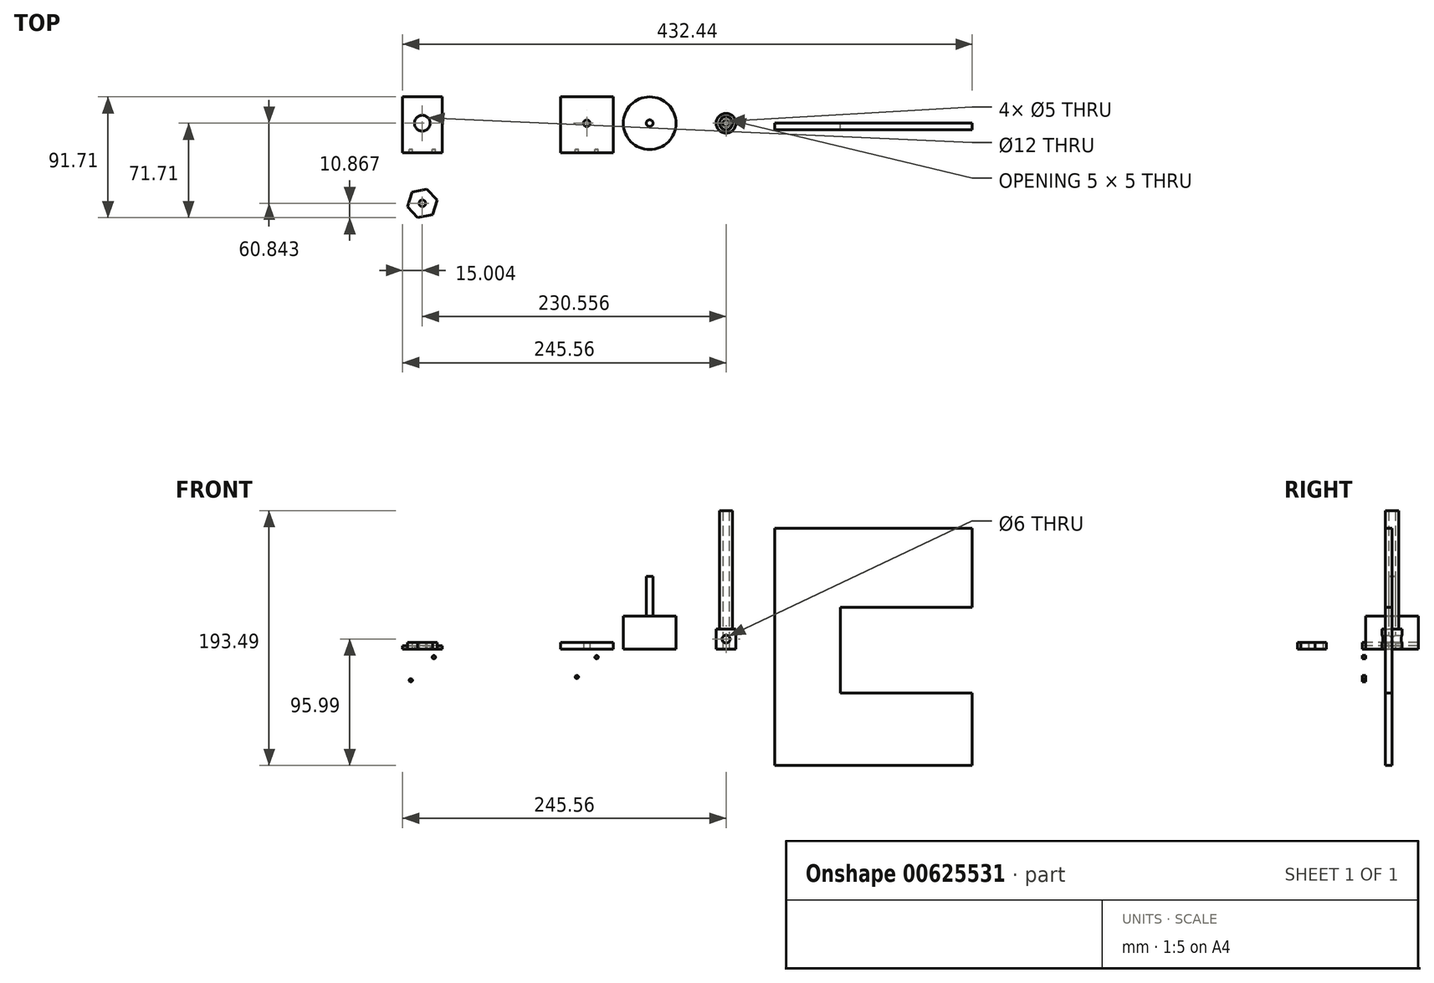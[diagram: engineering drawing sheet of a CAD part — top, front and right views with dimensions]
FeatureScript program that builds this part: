
annotation { "Feature Type Name" : "Feature", "Feature Type Description" : "" }
export const myFeature = defineFeature(function(context is Context, id is Id, definition is map)
    precondition{}
    {
        {
            var Q0;
            Q0=qCreatedBy(makeId("Top.planeOp"),FACE);
            var sketch = newSketch(context, id + "F0", { "sketchPlane" : qUnion([Q0])});
            skCircle(sketch, "E0", {"center": v(0, 0) * mm, "radius": 2.5 * mm});
            skCircle(sketch, "E1", {"center": v(0, 0) * mm, "radius": 7.5 * mm});
            skLineSegment(sketch, "E2", {"start": v(-20, 7.5) * mm, "end": v(20, 7.5) * mm});
            skCircle(sketch, "E3", {"center": v(-57.97, 0) * mm, "radius": 20 * mm});
            skLineSegment(sketch, "E4.bottom", {"start": v(-125.74, 20) * mm, "end": v(-85.74, 20) * mm});
            skLineSegment(sketch, "E4.top", {"start": v(-125.74, -20) * mm, "end": v(-85.74, -20) * mm});
            skLineSegment(sketch, "E4.left", {"start": v(-125.74, 20) * mm, "end": v(-125.74, -20) * mm});
            skLineSegment(sketch, "E4.right", {"start": v(-85.74, 20) * mm, "end": v(-85.74, -20) * mm});
            skPoint(sketch, "E4.middle", {"position": v(-105.74, 0) * mm});
            skCircle(sketch, "E5", {"center": v(-105.74, 0) * mm, "radius": 2.5 * mm});
            skLineSegment(sketch, "E6.bottom", {"start": v(-215.56, 20) * mm, "end": v(-245.56, 20) * mm});
            skLineSegment(sketch, "E6.top", {"start": v(-215.56, -20) * mm, "end": v(-245.56, -20) * mm});
            skLineSegment(sketch, "E6.left", {"start": v(-215.56, 20) * mm, "end": v(-215.56, -20) * mm});
            skLineSegment(sketch, "E6.right", {"start": v(-245.56, 20) * mm, "end": v(-245.56, -20) * mm});
            skCircle(sketch, "E7", {"center": v(-230.56, 0) * mm, "radius": 6 * mm});
            skPoint(sketch, "E7.centerSnap0", {"position": v(-230.56, 20) * mm});
            skCircle(sketch, "E8.cCircle", {"center": v(-230.56, -60.84) * mm, "radius": 9.88 * mm, "construction": true});
            skLineSegment(sketch, "E8.0", {"start": v(-219.4, -58.45) * mm, "end": v(-222.9, -69.3) * mm});
            skLineSegment(sketch, "E8.1", {"start": v(-222.9, -69.3) * mm, "end": v(-234.06, -71.7) * mm});
            skLineSegment(sketch, "E8.2", {"start": v(-234.06, -71.7) * mm, "end": v(-241.71, -63.24) * mm});
            skLineSegment(sketch, "E8.3", {"start": v(-241.71, -63.24) * mm, "end": v(-238.21, -52.38) * mm});
            skLineSegment(sketch, "E8.4", {"start": v(-238.21, -52.38) * mm, "end": v(-227.05, -49.98) * mm});
            skLineSegment(sketch, "E8.5", {"start": v(-227.05, -49.98) * mm, "end": v(-219.4, -58.45) * mm});
            skPoint(sketch, "E8.0.midPoint", {"position": v(-221.15, -63.88) * mm});
            skCircle(sketch, "E9", {"center": v(-230.56, -60.84) * mm, "radius": 2.5 * mm});
            skSolve(sketch);
        }
        {
            var Q0;
            Q0=makeQuery(id+"F0.imprint","IMPRINT",FACE,{"disambiguationData":[TD([[makeQuery(id+"F0.imprint","IMPRINT",EDGE,{"derivedFrom":sQuery(id+"F0.wireOp",EDGE,"E0")}),-1.0]])]});
            extrude(context, id + "F1", {"entities" : qUnion([Q0]), "depth" : 15 * mm, "offsetDistance" : 25 * mm});
        }
        {
            var Q0;
            Q0=makeQuery(id+"F1.opExtrude","CAP_FACE",FACE,{"disambiguationData":[OSD([sQuery(id+"F0.wireOp",EDGE,"E0"),sQuery(id+"F0.wireOp",EDGE,"E1")])],"isStart":false});
            var sketch = newSketch(context, id + "F2", { "sketchPlane" : qUnion([Q0])});
            skCircle(sketch, "E10", {"center": v(0, 0) * mm, "radius": 5 * mm});
            skSolve(sketch);
        }
        {
            var Q0;
            Q0=makeQuery(id+"F2.imprint","IMPRINT",FACE,{"disambiguationData":[TD([[makeQuery(id+"F2.imprint","IMPRINT",EDGE,{"derivedFrom":sQuery(id+"F2.wireOp",EDGE,"E10")}),1.0]])]});
            extrude(context, id + "F3", {"entities" : qUnion([Q0]), "operationType" : NewBodyOperationType.ADD, "depth" : 90 * mm, "offsetDistance" : 25 * mm});
        }
        {
            var Q0;
            Q0=sQuery(id+"F0.wireOp",EDGE,"E2");
            extrude(context, id + "F4", {"bodyType" : ToolBodyType.SURFACE, "surfaceEntities" : qUnion([Q0]), "depth" : 15 * mm, "offsetDistance" : 25 * mm});
        }
        {
            var Q0;
            Q0=makeQuery(id+"F4.opExtrude","SWEPT_FACE",FACE,{"disambiguationData":[OSD([sQuery(id+"F0.wireOp",EDGE,"E2")])]});
            var sketch = newSketch(context, id + "F5", { "sketchPlane" : qUnion([Q0])});
            skCircle(sketch, "E11", {"center": v(0, 7.5) * mm, "radius": 3 * mm});
            skPoint(sketch, "E11.centerSnap0", {"position": v(-20, 7.5) * mm});
            skSolve(sketch);
        }
        {
            var Q0;
            Q0=makeQuery(id+"F5.imprint","IMPRINT",FACE,{"disambiguationData":[TD([[makeQuery(id+"F5.imprint","IMPRINT",EDGE,{"derivedFrom":sQuery(id+"F5.wireOp",EDGE,"E11")}),1.0]])]});
            extrude(context, id + "F6", {"entities" : qUnion([Q0]), "operationType" : NewBodyOperationType.REMOVE, "endBound" : BoundingType.THROUGH_ALL, "depth" : 25 * mm, "offsetDistance" : 25 * mm});
        }
        {
            var Q0;
            Q0=makeQuery(id+"F0.imprint","IMPRINT",FACE,{"disambiguationData":[TD([[makeQuery(id+"F0.imprint","IMPRINT",EDGE,{"derivedFrom":sQuery(id+"F0.wireOp",EDGE,"E3")}),1.0]])]});
            extrude(context, id + "F7", {"entities" : qUnion([Q0]), "depth" : 25 * mm, "offsetDistance" : 25 * mm});
        }
        {
            var Q0;
            Q0=makeQuery(id+"F7.opExtrude","CAP_FACE",FACE,{"disambiguationData":[OSD([sQuery(id+"F0.wireOp",EDGE,"E3")])],"isStart":false});
            var sketch = newSketch(context, id + "F8", { "sketchPlane" : qUnion([Q0])});
            skCircle(sketch, "E12", {"center": v(-57.97, 0) * mm, "radius": 2.5 * mm});
            skSolve(sketch);
        }
        {
            var Q0;
            Q0=makeQuery(id+"F8.imprint","IMPRINT",FACE,{"disambiguationData":[TD([[makeQuery(id+"F8.imprint","IMPRINT",EDGE,{"derivedFrom":sQuery(id+"F8.wireOp",EDGE,"E12")}),1.0]])]});
            extrude(context, id + "F9", {"entities" : qUnion([Q0]), "operationType" : NewBodyOperationType.ADD, "depth" : 30 * mm, "offsetDistance" : 25 * mm});
        }
        {
            var Q0;
            Q0=makeQuery(id+"F0.imprint","IMPRINT",FACE,{"disambiguationData":[TD([[makeQuery(id+"F0.imprint","IMPRINT",EDGE,{"derivedFrom":sQuery(id+"F0.wireOp",EDGE,"E4.bottom")}),-1.0]])]});
            extrude(context, id + "F10", {"entities" : qUnion([Q0]), "depth" : 5 * mm, "offsetDistance" : 25 * mm});
        }
        {
            var Q0;
            Q0=makeQuery(id+"F10.opExtrude","CAP_FACE",FACE,{"disambiguationData":[OSD([sQuery(id+"F0.wireOp",EDGE,"E4.bottom"),sQuery(id+"F0.wireOp",EDGE,"E4.top"),sQuery(id+"F0.wireOp",EDGE,"E4.left"),sQuery(id+"F0.wireOp",EDGE,"E4.right"),sQuery(id+"F0.wireOp",EDGE,"E5")])],"isStart":false});
            var sketch = newSketch(context, id + "F11", { "sketchPlane" : qUnion([Q0])});
            skLineSegment(sketch, "E13.bottom", {"start": v(-125.74, -20) * mm, "end": v(-85.74, -20) * mm});
            skLineSegment(sketch, "E13.top", {"start": v(-125.74, -22.5) * mm, "end": v(-85.74, -22.5) * mm});
            skLineSegment(sketch, "E13.left", {"start": v(-125.74, -20) * mm, "end": v(-125.74, -22.5) * mm});
            skLineSegment(sketch, "E13.right", {"start": v(-85.74, -20) * mm, "end": v(-85.74, -22.5) * mm});
            skSolve(sketch);
        }
        {
            var Q0;
            Q0=makeQuery(id+"F11.imprint","IMPRINT",FACE,{"disambiguationData":[TD([[makeQuery(id+"F11.imprint","IMPRINT",EDGE,{"derivedFrom":sQuery(id+"F11.wireOp",EDGE,"E13.bottom")}),-1.0]])]});
            extrude(context, id + "F12", {"entities" : qUnion([Q0]), "operationType" : NewBodyOperationType.ADD, "oppositeDirection" : true, "depth" : 32.5 * mm, "offsetDistance" : 25 * mm});
        }
        {
            var Q0;
            Q0=qCreatedBy(makeId("Front.planeOp"),FACE);
            var sketch = newSketch(context, id + "F13", { "sketchPlane" : qUnion([Q0])});
            skLineSegment(sketch, "E14.bottom", {"start": v(36.88, 91.5) * mm, "end": v(186.88, 91.5) * mm});
            skLineSegment(sketch, "E14.top", {"start": v(36.88, -88.5) * mm, "end": v(186.88, -88.5) * mm});
            skLineSegment(sketch, "E14.left", {"start": v(36.88, 91.5) * mm, "end": v(36.88, -88.5) * mm});
            skLineSegment(sketch, "E14.right", {"start": v(186.88, 91.5) * mm, "end": v(186.88, -88.5) * mm});
            skLineSegment(sketch, "E15", {"start": v(186.88, 31.5) * mm, "end": v(86.88, 31.5) * mm});
            skLineSegment(sketch, "E16", {"start": v(186.88, -33.5) * mm, "end": v(86.88, -33.5) * mm});
            skLineSegment(sketch, "E17", {"start": v(86.88, 31.5) * mm, "end": v(86.88, -33.5) * mm});
            skLineSegment(sketch, "E18.bottom", {"start": v(272.35, 206.17) * mm, "end": v(332.35, 206.17) * mm});
            skLineSegment(sketch, "E18.top", {"start": v(272.35, 156.17) * mm, "end": v(332.35, 156.17) * mm});
            skLineSegment(sketch, "E18.left", {"start": v(272.35, 206.17) * mm, "end": v(272.35, 156.17) * mm});
            skLineSegment(sketch, "E18.right", {"start": v(332.35, 206.17) * mm, "end": v(332.35, 156.17) * mm});
            skCircle(sketch, "E19", {"center": v(322.35, 196.17) * mm, "radius": 3 * mm});
            skLineSegment(sketch, "E20", {"start": v(272.35, 181.17) * mm, "end": v(332.35, 181.17) * mm, "construction": true});
            skLineSegment(sketch, "E21", {"start": v(302.35, 156.17) * mm, "end": v(302.35, 206.17) * mm, "construction": true});
            skCircle(sketch, "E22.MirrorC", {"center": v(282.35, 196.17) * mm, "radius": 3 * mm});
            skCircle(sketch, "E23.MirrorC", {"center": v(282.35, 166.17) * mm, "radius": 3 * mm});
            skCircle(sketch, "E24.MirrorC", {"center": v(322.35, 166.17) * mm, "radius": 3 * mm});
            skSolve(sketch);
        }
        {
            var Q0;
            {var subQ1=sQuery(id+"F13.wireOp",EDGE,"E14.bottom");Q0=makeQuery(id+"F13.imprint","IMPRINT",FACE,{"disambiguationData":[TD([[makeQuery(id+"F13.imprint","IMPRINT",EDGE,{"derivedFrom":subQ1}),-1.0]])]});}
            extrude(context, id + "F14", {"entities" : qUnion([Q0]), "depth" : 5 * mm, "offsetDistance" : 25 * mm});
        }
        {
            var Q0;
            Q0=makeQuery(id+"F14.opExtrude","CAP_FACE",FACE,{"disambiguationData":[OSD([sQuery(id+"F13.wireOp",EDGE,"E14.bottom"),sQuery(id+"F13.wireOp",EDGE,"E14.top"),sQuery(id+"F13.wireOp",EDGE,"E14.left"),sQuery(id+"F13.wireOp",EDGE,"E14.right"),sQuery(id+"F13.wireOp",EDGE,"E15"),sQuery(id+"F13.wireOp",EDGE,"E16"),sQuery(id+"F13.wireOp",EDGE,"E17")])],"isStart":false});
            var sketch = newSketch(context, id + "F15", { "sketchPlane" : qUnion([Q0])});
            skLineSegment(sketch, "E25", {"start": v(186.88, 59) * mm, "end": v(86.88, 59) * mm});
            skLineSegment(sketch, "E26", {"start": v(86.88, 59) * mm, "end": v(86.88, 31.5) * mm});
            skLineSegment(sketch, "E27", {"start": v(186.88, -33.5) * mm, "end": v(86.88, -33.5) * mm});
            skLineSegment(sketch, "E28", {"start": v(86.88, -33.5) * mm, "end": v(86.88, -33.5) * mm});
            skLineSegment(sketch, "E29", {"start": v(86.88, 59) * mm, "end": v(86.88, 91.5) * mm});
            skLineSegment(sketch, "E30", {"start": v(86.88, 91.5) * mm, "end": v(86.88, -88.5) * mm});
            skSolve(sketch);
        }
        {
            var Q0;
            Q0=makeQuery(id+"F0.imprint","IMPRINT",FACE,{"disambiguationData":[TD([[makeQuery(id+"F0.imprint","IMPRINT",EDGE,{"derivedFrom":sQuery(id+"F0.wireOp",EDGE,"E6.bottom")}),1.0]])]});
            extrude(context, id + "F16", {"entities" : qUnion([Q0]), "depth" : 2.5 * mm, "offsetDistance" : 25 * mm});
        }
        {
            var Q0;
            Q0=makeQuery(id+"F16.opExtrude","CAP_FACE",FACE,{"disambiguationData":[OSD([sQuery(id+"F0.wireOp",EDGE,"E6.bottom"),sQuery(id+"F0.wireOp",EDGE,"E6.top"),sQuery(id+"F0.wireOp",EDGE,"E6.left"),sQuery(id+"F0.wireOp",EDGE,"E6.right"),sQuery(id+"F0.wireOp",EDGE,"E7")])],"isStart":false});
            var sketch = newSketch(context, id + "F17", { "sketchPlane" : qUnion([Q0])});
            skLineSegment(sketch, "E31.bottom", {"start": v(-245.56, -20) * mm, "end": v(-215.56, -20) * mm});
            skLineSegment(sketch, "E31.top", {"start": v(-245.56, -22.5) * mm, "end": v(-215.56, -22.5) * mm});
            skLineSegment(sketch, "E31.left", {"start": v(-245.56, -20) * mm, "end": v(-245.56, -22.5) * mm});
            skLineSegment(sketch, "E31.right", {"start": v(-215.56, -20) * mm, "end": v(-215.56, -22.5) * mm});
            skSolve(sketch);
        }
        {
            var Q0;
            Q0=makeQuery(id+"F17.imprint","IMPRINT",FACE,{"disambiguationData":[TD([[makeQuery(id+"F17.imprint","IMPRINT",EDGE,{"derivedFrom":sQuery(id+"F17.wireOp",EDGE,"E31.bottom")}),1.0]])]});
            extrude(context, id + "F18", {"entities" : qUnion([Q0]), "operationType" : NewBodyOperationType.ADD, "oppositeDirection" : true, "depth" : 32.5 * mm, "offsetDistance" : 25 * mm});
        }
        {
            var Q0;
            Q0=makeQuery(id+"F0.imprint","IMPRINT",FACE,{"disambiguationData":[TD([[makeQuery(id+"F0.imprint","IMPRINT",EDGE,{"derivedFrom":sQuery(id+"F0.wireOp",EDGE,"E8.0")}),-1.0]])]});
            extrude(context, id + "F19", {"entities" : qUnion([Q0]), "depth" : 5 * mm, "offsetDistance" : 25 * mm});
        }
        {
            var Q0;
            Q0=makeQuery(id+"F12.opExtrude","SWEPT_FACE",FACE,{"disambiguationData":[OSD([sQuery(id+"F11.wireOp",EDGE,"E13.bottom")])]});
            var sketch = newSketch(context, id + "F20", { "sketchPlane" : qUnion([Q0])});
            skCircle(sketch, "E32", {"center": v(113.24, -6.25) * mm, "radius": 1.25 * mm});
            skLineSegment(sketch, "E33", {"start": v(105.74, 0) * mm, "end": v(105.74, -27.5) * mm, "construction": true});
            skLineSegment(sketch, "E34", {"start": v(125.74, -13.75) * mm, "end": v(85.74, -13.75) * mm, "construction": true});
            skCircle(sketch, "E35.MirrorC", {"center": v(98.24, -6.25) * mm, "radius": 1.25 * mm});
            skCircle(sketch, "E36.MirrorC", {"center": v(98.24, -21.25) * mm, "radius": 1.25 * mm});
            skCircle(sketch, "E37.MirrorC", {"center": v(113.24, -21.25) * mm, "radius": 1.25 * mm});
            skSolve(sketch);
        }
        {
            var Q0;
            Q0=makeQuery(id+"F20.imprint","IMPRINT",FACE,{"disambiguationData":[TD([[makeQuery(id+"F20.imprint","IMPRINT",EDGE,{"derivedFrom":sQuery(id+"F20.wireOp",EDGE,"E35.MirrorC")}),-1.0]])]});
            var Q1;
            Q1=makeQuery(id+"F20.imprint","IMPRINT",FACE,{"disambiguationData":[TD([[makeQuery(id+"F20.imprint","IMPRINT",EDGE,{"derivedFrom":sQuery(id+"F20.wireOp",EDGE,"E32")}),1.0]])]});
            var Q2;
            Q2=makeQuery(id+"F20.imprint","IMPRINT",FACE,{"disambiguationData":[TD([[makeQuery(id+"F20.imprint","IMPRINT",EDGE,{"derivedFrom":sQuery(id+"F20.wireOp",EDGE,"E37.MirrorC")}),-1.0]])]});
            var Q3;
            Q3=makeQuery(id+"F20.imprint","IMPRINT",FACE,{"disambiguationData":[TD([[makeQuery(id+"F20.imprint","IMPRINT",EDGE,{"derivedFrom":sQuery(id+"F20.wireOp",EDGE,"E36.MirrorC")}),1.0]])]});
            extrude(context, id + "F21", {"entities" : qUnion([Q0, Q1, Q2, Q3]), "operationType" : NewBodyOperationType.REMOVE, "endBound" : BoundingType.UP_TO_NEXT, "oppositeDirection" : true, "depth" : 25 * mm, "offsetDistance" : 25 * mm});
        }
        {
            var Q0;
            Q0=makeQuery(id+"F18.opExtrude","SWEPT_FACE",FACE,{"disambiguationData":[OSD([sQuery(id+"F17.wireOp",EDGE,"E31.bottom")])]});
            var sketch = newSketch(context, id + "F22", { "sketchPlane" : qUnion([Q0])});
            skLineSegment(sketch, "E38", {"start": v(230.56, 0) * mm, "end": v(230.56, -30) * mm, "construction": true});
            skLineSegment(sketch, "E39", {"start": v(215.56, -15) * mm, "end": v(245.56, -15) * mm, "construction": true});
            skCircle(sketch, "E40", {"center": v(239.3, -6.25) * mm, "radius": 1.25 * mm});
            skCircle(sketch, "E41.MirrorC", {"center": v(221.8, -6.25) * mm, "radius": 1.25 * mm});
            skCircle(sketch, "E42.MirrorC", {"center": v(221.8, -23.75) * mm, "radius": 1.25 * mm});
            skCircle(sketch, "E43.MirrorC", {"center": v(239.3, -23.75) * mm, "radius": 1.25 * mm});
            skSolve(sketch);
        }
        {
            var Q0;
            Q0=makeQuery(id+"F22.imprint","IMPRINT",FACE,{"disambiguationData":[TD([[makeQuery(id+"F22.imprint","IMPRINT",EDGE,{"derivedFrom":sQuery(id+"F22.wireOp",EDGE,"E41.MirrorC")}),-1.0]])]});
            var Q1;
            Q1=makeQuery(id+"F22.imprint","IMPRINT",FACE,{"disambiguationData":[TD([[makeQuery(id+"F22.imprint","IMPRINT",EDGE,{"derivedFrom":sQuery(id+"F22.wireOp",EDGE,"E42.MirrorC")}),1.0]])]});
            var Q2;
            Q2=makeQuery(id+"F22.imprint","IMPRINT",FACE,{"disambiguationData":[TD([[makeQuery(id+"F22.imprint","IMPRINT",EDGE,{"derivedFrom":sQuery(id+"F22.wireOp",EDGE,"E43.MirrorC")}),-1.0]])]});
            var Q3;
            Q3=makeQuery(id+"F22.imprint","IMPRINT",FACE,{"disambiguationData":[TD([[makeQuery(id+"F22.imprint","IMPRINT",EDGE,{"derivedFrom":sQuery(id+"F22.wireOp",EDGE,"E40")}),1.0]])]});
            extrude(context, id + "F23", {"entities" : qUnion([Q0, Q1, Q2, Q3]), "operationType" : NewBodyOperationType.REMOVE, "endBound" : BoundingType.UP_TO_NEXT, "oppositeDirection" : true, "depth" : 25 * mm, "offsetDistance" : 25 * mm});
        }
    });
